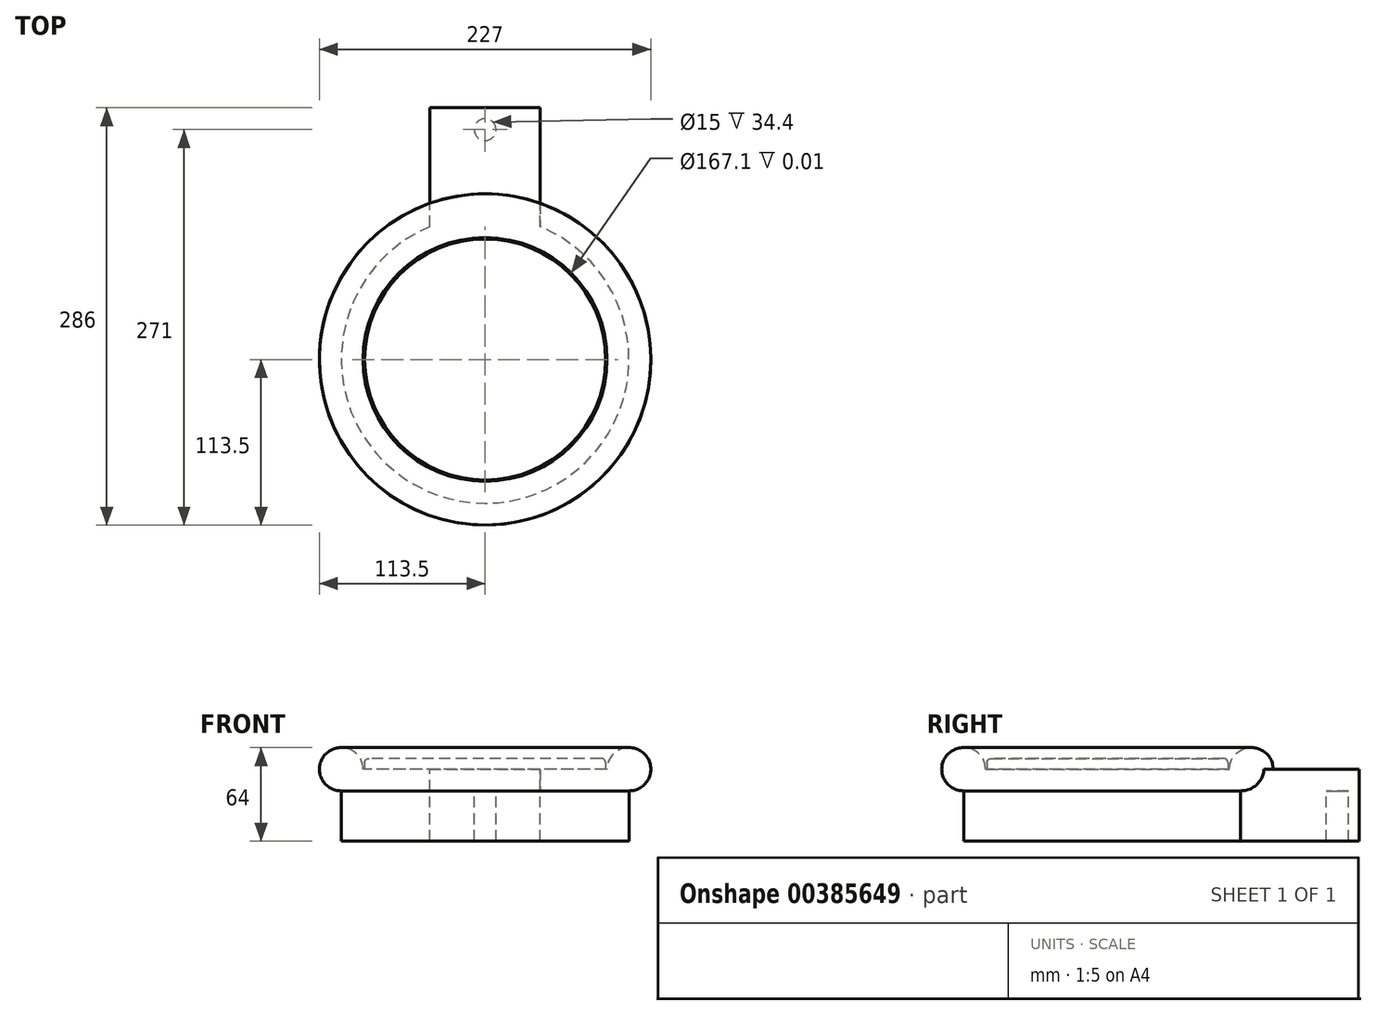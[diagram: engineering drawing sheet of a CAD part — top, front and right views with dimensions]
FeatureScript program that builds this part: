
annotation { "Feature Type Name" : "Feature", "Feature Type Description" : "" }
export const myFeature = defineFeature(function(context is Context, id is Id, definition is map)
    precondition{}
    {
        {
            var Q0;
            Q0=qCreatedBy(makeId("Top.planeOp"),FACE);
            var sketch = newSketch(context, id + "F0", { "sketchPlane" : qUnion([Q0])});
            skCircle(sketch, "E0", {"center": v(0, 0) * mm, "radius": 113.5 * mm});
            skCircle(sketch, "E1", {"center": v(0, 0) * mm, "radius": 98.53 * mm});
            skCircle(sketch, "E2", {"center": v(0, 0) * mm, "radius": 83.55 * mm});
            skCircle(sketch, "E3", {"center": v(0, 0) * mm, "radius": 82.55 * mm});
            skLineSegment(sketch, "E4.top", {"start": v(-37.83, 172.5) * mm, "end": v(37.83, 172.5) * mm});
            skLineSegment(sketch, "E4.left", {"start": v(-37.83, 90.97) * mm, "end": v(-37.83, 172.5) * mm});
            skLineSegment(sketch, "E4.right", {"start": v(37.83, 90.97) * mm, "end": v(37.83, 172.5) * mm});
            skLineSegment(sketch, "E5", {"start": v(0, 0) * mm, "end": v(0, -113.5) * mm, "construction": true});
            skLineSegment(sketch, "E6", {"start": v(0, -83.55) * mm, "end": v(0, -98.53) * mm, "construction": true});
            skLineSegment(sketch, "E7", {"start": v(-6.7, -98.53) * mm, "end": v(6.7, -98.53) * mm, "construction": true});
            skCircle(sketch, "E8", {"center": v(0, 157.5) * mm, "radius": 7.5 * mm});
            skSolve(sketch);
        }
        {
            assignVariable(context, id + "F1", {"name" : "raio", "anyValue" : 14.8});
        }
        {
            assignVariable(context, id + "F2", {"name" : "alt", "anyValue" : 64 - 2 * 14.8});
        }
        {
            var Q0;
            {var subQ5=sQuery(id+"F0.wireOp",EDGE,"E4.top");Q0=makeQuery(id+"F0.imprint","IMPRINT",FACE,{"disambiguationData":[TD([[makeQuery(id+"F0.imprint","IMPRINT",EDGE,{"derivedFrom":subQ5}),-1.0]])]});}
            var Q1;
            {var subQ0=sQuery(id+"F0.wireOp",EDGE,"E4.left");var subQ1=sQuery(id+"F0.wireOp",EDGE,"E0");var subQ2=makeQuery(id+"F0.imprint","INTERSECT",VERTEX,{"derivedFrom":[subQ1,subQ0]});Q1=makeQuery(id+"F0.imprint","IMPRINT",FACE,{"disambiguationData":[TD([[makeQuery(id+"F0.imprint","IMPRINT",EDGE,{"disambiguationData":[TD([[subQ2,1.0]])],"derivedFrom":subQ1}),1.0]])]});}
            var Q2;
            Q2=makeQuery(id+"F0.imprint","IMPRINT",FACE,{"disambiguationData":[TD([[makeQuery(id+"F0.imprint","IMPRINT",EDGE,{"derivedFrom":sQuery(id+"F0.wireOp",EDGE,"E2")}),-1.0]])]});
            var Q3;
            Q3=makeQuery(id+"F0.imprint","IMPRINT",FACE,{"disambiguationData":[TD([[makeQuery(id+"F0.imprint","IMPRINT",EDGE,{"derivedFrom":sQuery(id+"F0.wireOp",EDGE,"E2")}),1.0]])]});
            var Q4;
            Q4=makeQuery(id+"F0.imprint","IMPRINT",FACE,{"disambiguationData":[TD([[makeQuery(id+"F0.imprint","IMPRINT",EDGE,{"derivedFrom":sQuery(id+"F0.wireOp",EDGE,"E3")}),1.0]])]});
            extrude(context, id + "F3", {"entities" : qUnion([Q0, Q1, Q2, Q3, Q4]), "oppositeDirection" : true, "depth" : (getVariable(context, 'alt')) * mm});
        }
        {
            var Q0;
            {var subQ0=sQuery(id+"F0.wireOp",EDGE,"E4.left");var subQ1=sQuery(id+"F0.wireOp",EDGE,"E0");var subQ2=makeQuery(id+"F0.imprint","INTERSECT",VERTEX,{"derivedFrom":[subQ1,subQ0]});Q0=makeQuery(id+"F0.imprint","IMPRINT",FACE,{"disambiguationData":[TD([[makeQuery(id+"F0.imprint","IMPRINT",EDGE,{"disambiguationData":[TD([[subQ2,-1.0]])],"derivedFrom":subQ1}),1.0]])]});}
            var Q1;
            Q1=makeQuery(id+"F0.imprint","IMPRINT",FACE,{"disambiguationData":[TD([[makeQuery(id+"F0.imprint","IMPRINT",EDGE,{"derivedFrom":sQuery(id+"F0.wireOp",EDGE,"E2")}),-1.0]])]});
            var Q2;
            Q2=makeQuery(id+"F0.imprint","IMPRINT",FACE,{"disambiguationData":[TD([[makeQuery(id+"F0.imprint","IMPRINT",EDGE,{"derivedFrom":sQuery(id+"F0.wireOp",EDGE,"E2")}),1.0]])]});
            var Q3;
            Q3=makeQuery(id+"F0.imprint","IMPRINT",FACE,{"disambiguationData":[TD([[makeQuery(id+"F0.imprint","IMPRINT",EDGE,{"derivedFrom":sQuery(id+"F0.wireOp",EDGE,"E3")}),1.0]])]});
            var Q4;
            {var subQ0=sQuery(id+"F0.wireOp",EDGE,"E4.left");var subQ1=sQuery(id+"F0.wireOp",EDGE,"E0");var subQ2=makeQuery(id+"F0.imprint","INTERSECT",VERTEX,{"derivedFrom":[subQ1,subQ0]});Q4=makeQuery(id+"F0.imprint","IMPRINT",FACE,{"disambiguationData":[TD([[makeQuery(id+"F0.imprint","IMPRINT",EDGE,{"disambiguationData":[TD([[subQ2,1.0]])],"derivedFrom":subQ1}),1.0]])]});}
            var Q5;
            {var subQ5=sQuery(id+"F0.wireOp",EDGE,"E4.top");Q5=makeQuery(id+"F0.imprint","IMPRINT",FACE,{"disambiguationData":[TD([[makeQuery(id+"F0.imprint","IMPRINT",EDGE,{"derivedFrom":subQ5}),-1.0]])]});}
            var Q6;
            {var subQ0=sQuery(id+"F0.wireOp",EDGE,"E8");var subQ1=sQuery(id+"F0.wireOp",EDGE,"E0");var subQ2=makeQuery(id+"F0.imprint","INTERSECT",VERTEX,{"disambiguationData":[OD(0.0)],"derivedFrom":[subQ1,subQ0]});Q6=makeQuery(id+"F0.imprint","IMPRINT",FACE,{"disambiguationData":[TD([[makeQuery(id+"F0.imprint","IMPRINT",EDGE,{"disambiguationData":[TD([[subQ2,-1.0]])],"derivedFrom":subQ1}),1.0]])]});}
            var Q7;
            {var subQ0=sQuery(id+"F0.wireOp",EDGE,"E8");var subQ1=sQuery(id+"F0.wireOp",EDGE,"E0");var subQ2=makeQuery(id+"F0.imprint","INTERSECT",VERTEX,{"disambiguationData":[OD(0.0)],"derivedFrom":[subQ1,subQ0]});Q7=makeQuery(id+"F0.imprint","IMPRINT",FACE,{"disambiguationData":[TD([[makeQuery(id+"F0.imprint","IMPRINT",EDGE,{"disambiguationData":[TD([[subQ2,-1.0]])],"derivedFrom":subQ1}),-1.0]])]});}
            var Q8;
            Q8=makeQuery(id+"F0.imprint","IMPRINT",FACE,{"disambiguationData":[TD([[makeQuery(id+"F0.imprint","IMPRINT",EDGE,{"derivedFrom":sQuery(id+"F0.wireOp",EDGE,"E8")}),1.0]])]});
            extrude(context, id + "F4", {"entities" : qUnion([Q0, Q1, Q2, Q3, Q4, Q5, Q6, Q7, Q8]), "operationType" : NewBodyOperationType.ADD, "depth" : (getVariable(context, 'raio')) * mm});
        }
        {
            var Q0;
            {var subQ0=sQuery(id+"F0.wireOp",EDGE,"E4.left");var subQ1=sQuery(id+"F0.wireOp",EDGE,"E0");var subQ2=makeQuery(id+"F0.imprint","INTERSECT",VERTEX,{"derivedFrom":[subQ1,subQ0]});Q0=makeQuery(id+"F0.imprint","IMPRINT",FACE,{"disambiguationData":[TD([[makeQuery(id+"F0.imprint","IMPRINT",EDGE,{"disambiguationData":[TD([[subQ2,-1.0]])],"derivedFrom":subQ1}),1.0]])]});}
            var Q1;
            Q1=makeQuery(id+"F0.imprint","IMPRINT",FACE,{"disambiguationData":[TD([[makeQuery(id+"F0.imprint","IMPRINT",EDGE,{"derivedFrom":sQuery(id+"F0.wireOp",EDGE,"E2")}),-1.0]])]});
            var Q2;
            {var subQ0=sQuery(id+"F0.wireOp",EDGE,"E4.left");var subQ1=sQuery(id+"F0.wireOp",EDGE,"E0");var subQ2=makeQuery(id+"F0.imprint","INTERSECT",VERTEX,{"derivedFrom":[subQ1,subQ0]});Q2=makeQuery(id+"F0.imprint","IMPRINT",FACE,{"disambiguationData":[TD([[makeQuery(id+"F0.imprint","IMPRINT",EDGE,{"disambiguationData":[TD([[subQ2,1.0]])],"derivedFrom":subQ1}),1.0]])]});}
            var Q3;
            {var subQ0=sQuery(id+"F0.wireOp",EDGE,"E8");var subQ1=sQuery(id+"F0.wireOp",EDGE,"E0");var subQ2=makeQuery(id+"F0.imprint","INTERSECT",VERTEX,{"disambiguationData":[OD(0.0)],"derivedFrom":[subQ1,subQ0]});Q3=makeQuery(id+"F0.imprint","IMPRINT",FACE,{"disambiguationData":[TD([[makeQuery(id+"F0.imprint","IMPRINT",EDGE,{"disambiguationData":[TD([[subQ2,-1.0]])],"derivedFrom":subQ1}),1.0]])]});}
            extrude(context, id + "F5", {"entities" : qUnion([Q0, Q1, Q2, Q3]), "operationType" : NewBodyOperationType.ADD, "depth" : (2 * getVariable(context, 'raio')) * mm, "hasSecondDirection" : true, "secondDirectionOppositeDirection" : false, "secondDirectionDepth" : (getVariable(context, 'raio')) * mm});
        }
        {
            var Q0;
            Q0=makeQuery(id+"F5.opExtrude","CAP_EDGE",EDGE,{"disambiguationData":[OSD([sQuery(id+"F0.wireOp",EDGE,"E0")])],"isStart":false});
            var Q1;
            Q1=makeQuery(id+"F5.opExtrude","CAP_EDGE",EDGE,{"disambiguationData":[OSD([sQuery(id+"F0.wireOp",EDGE,"E2")])],"isStart":false});
            var Q2;
            Q2=makeQuery(id+"F4.opExtrude","CAP_EDGE",EDGE,{"disambiguationData":[OSD([sQuery(id+"F0.wireOp",EDGE,"E0")])],"isStart":true});
            fillet(context, id + "F6", {"entities" : qUnion([Q0, Q1, Q2]), "radius" : 14.79 * mm, "tangentPropagation" : true, "allowEdgeOverflow" : false});
        }
        {
            var Q0;
            Q0=makeQuery(id+"F0.imprint","IMPRINT",FACE,{"disambiguationData":[TD([[makeQuery(id+"F0.imprint","IMPRINT",EDGE,{"derivedFrom":sQuery(id+"F0.wireOp",EDGE,"E3")}),1.0]])]});
            extrude(context, id + "F7", {"entities" : qUnion([Q0]), "depth" : 1.5 * (getVariable(context, 'raio')) * mm, "hasSecondDirection" : true, "secondDirectionOppositeDirection" : false, "secondDirectionDepth" : (getVariable(context, 'raio')) * mm});
        }
        {
            var Q0;
            Q0=makeQuery(id+"F7.opExtrude","CAP_EDGE",EDGE,{"disambiguationData":[OSD([sQuery(id+"F0.wireOp",EDGE,"E3")])],"isStart":false});
            fillet(context, id + "F8", {"entities" : qUnion([Q0]), "radius" : 3 * mm, "tangentPropagation" : true, "allowEdgeOverflow" : false});
        }
    });
